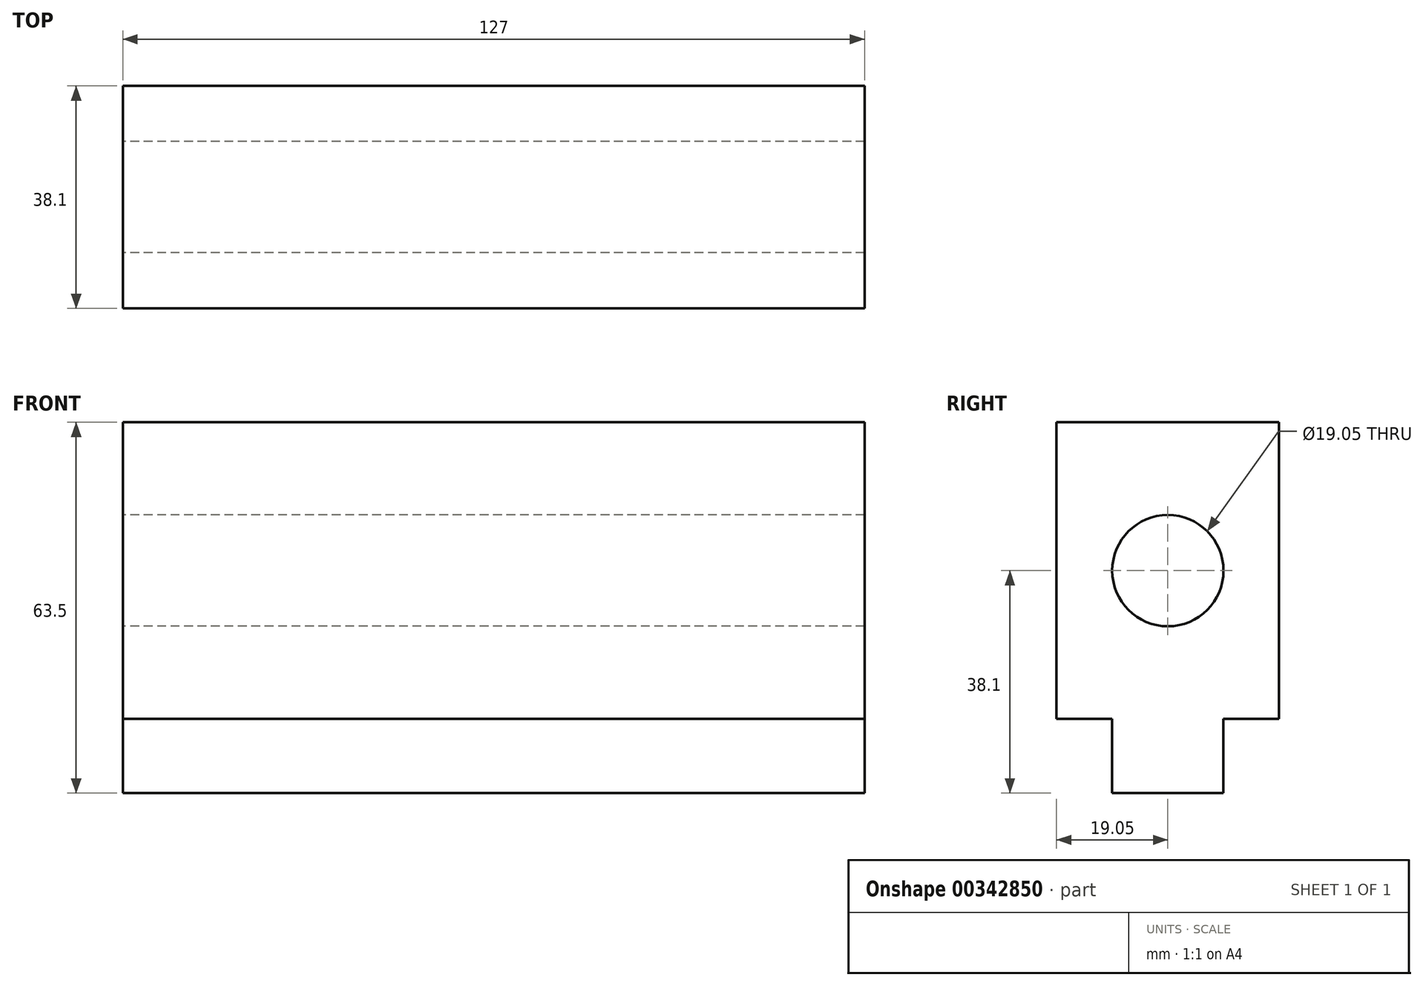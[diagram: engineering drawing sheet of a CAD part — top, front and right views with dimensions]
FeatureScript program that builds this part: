
annotation { "Feature Type Name" : "Feature", "Feature Type Description" : "" }
export const myFeature = defineFeature(function(context is Context, id is Id, definition is map)
    precondition{}
    {
        {
            var Q0;
            Q0=qCreatedBy(makeId("Right.planeOp"),FACE);
            var sketch = newSketch(context, id + "F0", { "sketchPlane" : qUnion([Q0])});
            skLineSegment(sketch, "E0.bottom", {"start": v(-9.52, -31.75) * mm, "end": v(9.52, -31.75) * mm});
            skLineSegment(sketch, "E0.top", {"start": v(-19.05, 31.75) * mm, "end": v(19.05, 31.75) * mm});
            skLineSegment(sketch, "E0.left", {"start": v(-19.05, -19.05) * mm, "end": v(-19.05, 31.75) * mm});
            skLineSegment(sketch, "E0.right", {"start": v(19.05, -19.05) * mm, "end": v(19.05, 31.75) * mm});
            skPoint(sketch, "E0.middle", {"position": v(0, 0) * mm});
            skLineSegment(sketch, "E1", {"start": v(-9.52, -31.75) * mm, "end": v(-9.52, -19.05) * mm});
            skLineSegment(sketch, "E2", {"start": v(9.52, -19.05) * mm, "end": v(9.52, -31.75) * mm});
            skLineSegment(sketch, "E3", {"start": v(-19.05, -19.05) * mm, "end": v(-9.52, -19.05) * mm});
            skLineSegment(sketch, "E4", {"start": v(9.52, -19.05) * mm, "end": v(19.05, -19.05) * mm});
            skPoint(sketch, "E5.orphan", {"position": v(19.05, -31.75) * mm});
            skPoint(sketch, "E6.orphan", {"position": v(-19.05, -31.75) * mm});
            skLineSegment(sketch, "E7", {"start": v(-19.05, 31.75) * mm, "end": v(-19.05, 6.35) * mm});
            skCircle(sketch, "E8", {"center": v(0, 6.35) * mm, "radius": 9.53 * mm});
            skSolve(sketch);
        }
        {
            var Q0;
            Q0 = qSketchRegion(id + "F0", true);
            extrude(context, id + "F1", {"entities" : qUnion([Q0]), "depth" : 127 * mm});
        }
    });
